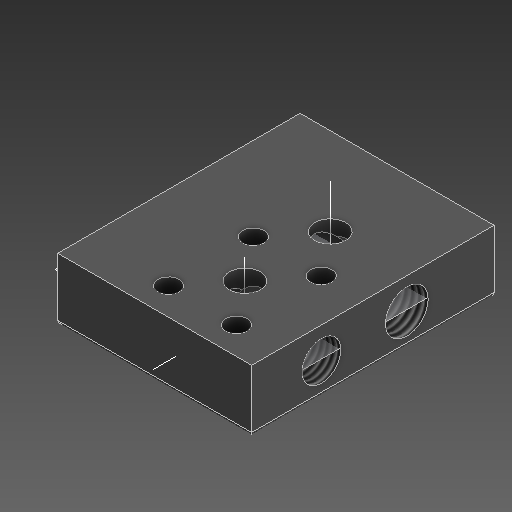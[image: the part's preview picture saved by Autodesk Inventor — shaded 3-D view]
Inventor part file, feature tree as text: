
AUTODESK INVENTOR PART (.ipt)
format: ipt  version: 2021 (Build 250183000, 183)  size: 302,592 bytes
history: native  units: in
note: dims shown in document units (in); Inventor stores cm internally (conversion verified against a paired STEP export)
features: other x12, direct_edit x5, hole x5, move_body x4, plane x3, sketch x3, extrude x2, thread x2, reference x2
ambient origin geometry x8: Origin, YZ Plane, XZ Plane, XY Plane, X Axis, Y Axis, Z Axis, Center Point
bodies: Solid1 (feature_tree)
feature tree (38):
  direct_edit  "Direct Edit1"
  plane  "Work Plane1"
  other  "Work Axis2"
  plane  "Work Plane2"
  extrude  "Extrusion1"  Depth=0.0591in TaperAngle=0.0deg
  plane  "Work Plane3"
  hole  "Hole2"  [1 undecoded]
  extrude  "Extrusion3"  Depth=1.9685in TaperAngle=0.0deg
  sketch  "Sketch4"  dims[d6=0.6184in d7=90.0deg d8=0.0in d9=0.0in d10=0.6299in]
  hole  "Hole6"  [1 undecoded]
  hole  "Hole7"  [1 undecoded]
  hole  "Hole10"  [1 undecoded]
  hole  "Hole12"  [1 undecoded]
  direct_edit  "Direct Edit4"
  direct_edit  "Direct Edit5"
  direct_edit  "Direct Edit6"
  direct_edit  "Direct Edit7"
  thread  "Thread1"  [1 undecoded]
  thread  "Thread3"  [1 undecoded]
  other  "Work Axis1"
  sketch  "Sketch3"  dims[d0=0.0in d1=0.0in d2=0.0591in d3=0.0in d4=0.0in d5=0.0591in]
  other  "Work Axis3"
  sketch  "Sketch6"  dims[d11=0.0in d12=0.0in d13=0.3937in d14=1.9685in d15=0.0in d16=0.315in d17=0.315in d20=0.2362in d28=0.2756in d29=0.2362in d30=0.1575in d31=0.0787in d32=90.0deg d33=1.9685in d34=0.8108in d35=0.4724in d36=1.3189in d37=0.0in d62=0.2362in d63=0.2362in d64=0.1575in d65=0.0787in d66=90.0deg d67=1.5123in d68=0.8108in d69=0.4331in d70=0.2362in d71=0.1575in d72=0.0787in d73=90.0deg d74=0.9449in d75=0.0in d90=0.315in d91=0.2362in d92=0.1575in d93=0.0787in d94=90.0deg d95=1.4961in d96=0.8108in d105=0.3937in d106=0.2362in d107=0.1575in d108=0.0787in d109=90.0deg d110=0.1575in d111=0.0in d112=-0.0394in d113=0.2362in d114=-0.0197in d115=-0.0394in d116=0.3937in d117=0.0in d120=0.3937in d121=0.0in d118=0.5635in d119=0.0295in d122=0.0295in d123=0.0148in]
  reference  "Reference1"
  reference  "Reference2"
  other  "Cut-Extrude26"
  move_body  "Move1"
  move_body  "Move2"
  move_body  "Move3"
  move_body  "Move4"
  parser-record x1  (decoder bookkeeping rows leaked as tree rows — omitted from the tree; the rows remain in map.json)
  other  "BodyV4.iam"
  other  "rotarynozzle:1"
  other  "iner_sleeve:1"
  other  "Size2"
  other  "Size3"
  other  "Size4"
  other  "Size5"
note: 7 required parameter values undecoded (feature->parameter linkage not recoverable at this tier; creation-order binding heuristic only, values carry confidence <= 0.55)
note: 1 file-system path scrubbed to <path> (originals preserved in map.json)
